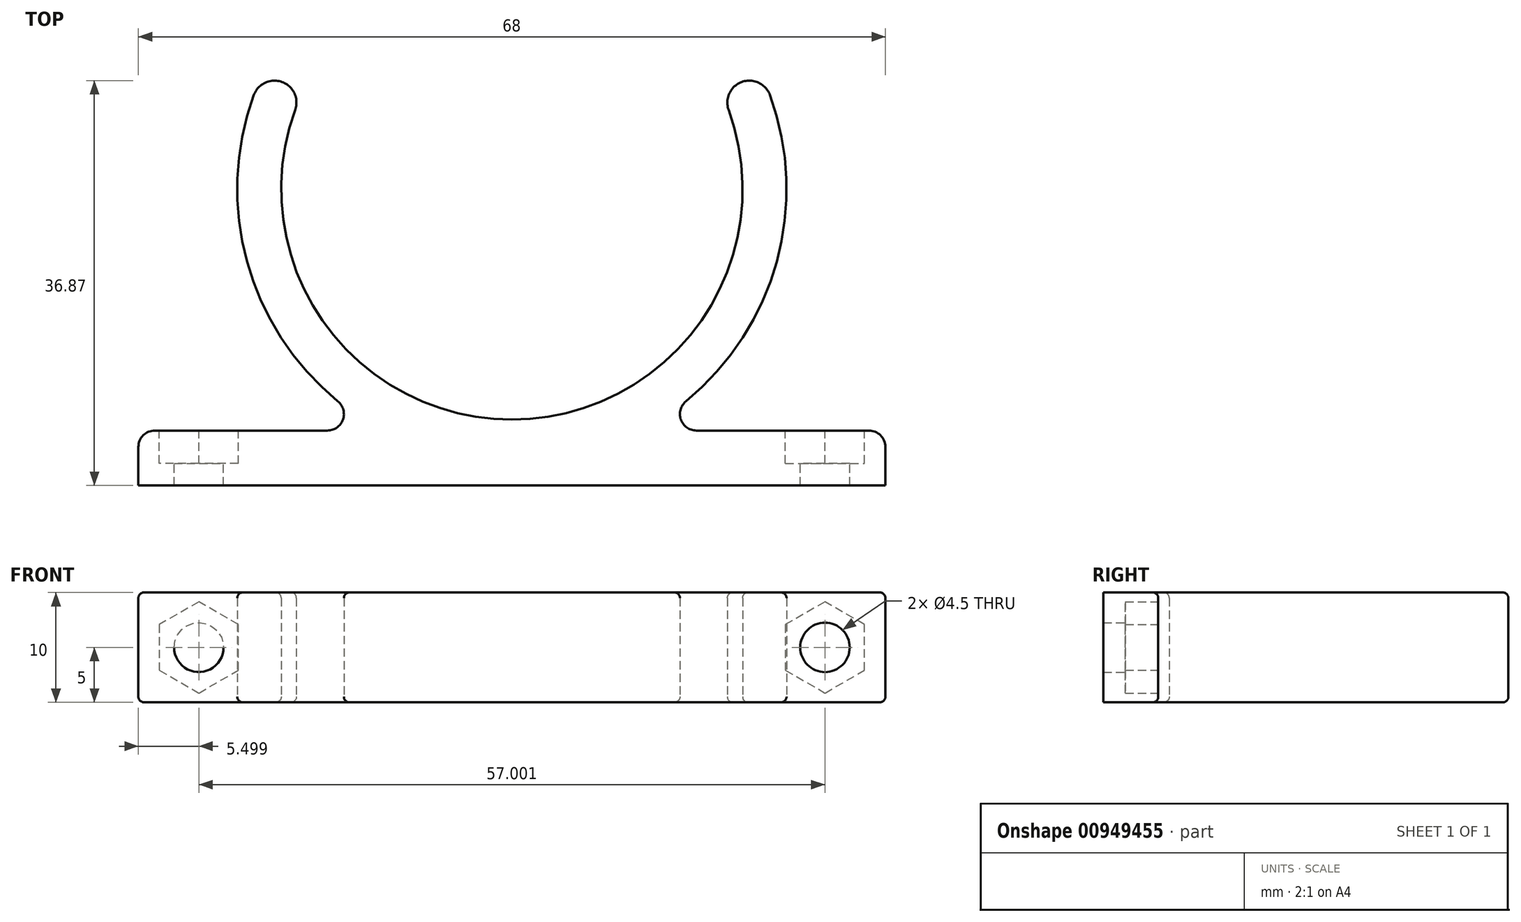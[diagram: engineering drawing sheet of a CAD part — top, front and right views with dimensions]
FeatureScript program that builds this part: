
annotation { "Feature Type Name" : "Feature", "Feature Type Description" : "" }
export const myFeature = defineFeature(function(context is Context, id is Id, definition is map)
    precondition{}
    {
        {
            var Q0;
            Q0=qCreatedBy(makeId("Top.planeOp"),FACE);
            var sketch = newSketch(context, id + "F0", { "sketchPlane" : qUnion([Q0])});
            skArc(sketch, "E0", {"start": v(19.73, 7.18) * mm, "mid": v(0, -21) * mm, "end": v(-19.73, 7.18) * mm});
            skLineSegment(sketch, "E1", {"start": v(0, 0) * mm, "end": v(19.73, 7.18) * mm, "construction": true});
            skLineSegment(sketch, "E2", {"start": v(0, 0) * mm, "end": v(-19.73, 7.18) * mm, "construction": true});
            skArc(sketch, "E3", {"start": v(15.84, -19.34) * mm, "mid": v(24.1, -6.61) * mm, "end": v(23.5, 8.55) * mm});
            skLineSegment(sketch, "E4", {"start": v(0, 0) * mm, "end": v(-23.5, 8.55) * mm, "construction": true});
            skLineSegment(sketch, "E5", {"start": v(0, 0) * mm, "end": v(23.5, 8.55) * mm, "construction": true});
            skLineSegment(sketch, "E6", {"start": v(-23.5, 8.55) * mm, "end": v(-19.73, 7.18) * mm});
            skLineSegment(sketch, "E7", {"start": v(23.5, 8.55) * mm, "end": v(19.73, 7.18) * mm});
            skLineSegment(sketch, "E8.bottom", {"start": v(34, -27) * mm, "end": v(-34, -27) * mm});
            skLineSegment(sketch, "E8.top", {"start": v(32.5, -22) * mm, "end": v(16.8, -22) * mm});
            skLineSegment(sketch, "E8.left", {"start": v(34, -27) * mm, "end": v(34, -23.5) * mm});
            skLineSegment(sketch, "E8.right", {"start": v(-34, -27) * mm, "end": v(-34, -23.5) * mm});
            skPoint(sketch, "E8.middle", {"position": v(0, -24.5) * mm});
            skArc(sketch, "E9", {"start": v(23.5, 8.55) * mm, "mid": v(20.93, 9.75) * mm, "end": v(19.73, 7.18) * mm});
            skArc(sketch, "E10", {"start": v(-23.5, 8.55) * mm, "mid": v(-20.93, 9.75) * mm, "end": v(-19.73, 7.18) * mm});
            skPoint(sketch, "E11.visualSharp", {"position": v(-34, -22) * mm});
            skArc(sketch, "E11.filletArc", {"start": v(-32.5, -22) * mm, "mid": v(-33.56, -22.44) * mm, "end": v(-34, -23.5) * mm});
            skPoint(sketch, "E12.visualSharp", {"position": v(34, -22) * mm});
            skArc(sketch, "E12.filletArc", {"start": v(34, -23.5) * mm, "mid": v(33.56, -22.44) * mm, "end": v(32.5, -22) * mm});
            skArc(sketch, "E13.filletArc", {"start": v(15.84, -19.34) * mm, "mid": v(15.38, -21) * mm, "end": v(16.8, -22) * mm});
            skArc(sketch, "E14", {"start": v(-23.5, 8.55) * mm, "mid": v(-24.1, -6.61) * mm, "end": v(-15.84, -19.34) * mm});
            skLineSegment(sketch, "E15", {"start": v(-32.5, -22) * mm, "end": v(-16.8, -22) * mm});
            skPoint(sketch, "E16.visualSharp", {"position": v(-11.87, -22) * mm});
            skArc(sketch, "E16.filletArc", {"start": v(-16.8, -22) * mm, "mid": v(-15.38, -21) * mm, "end": v(-15.84, -19.34) * mm});
            skSolve(sketch);
        }
        {
            var Q0;
            Q0=makeQuery(id+"F0.imprint","IMPRINT",FACE,{"disambiguationData":[TD([[makeQuery(id+"F0.imprint","IMPRINT",EDGE,{"derivedFrom":sQuery(id+"F0.wireOp",EDGE,"E0")}),1.0]])]});
            var Q1;
            Q1=makeQuery(id+"F0.imprint","IMPRINT",FACE,{"disambiguationData":[TD([[makeQuery(id+"F0.imprint","IMPRINT",EDGE,{"derivedFrom":sQuery(id+"F0.wireOp",EDGE,"E8.bottom")}),-1.0]])]});
            var Q2;
            {var subQ0=sQuery(id+"F0.wireOp",EDGE,"E8.top");var subQ1=sQuery(id+"F0.wireOp",EDGE,"E3");var subQ2=makeQuery(id+"F0.imprint","INTERSECT",VERTEX,{"disambiguationData":[OD(0.0)],"derivedFrom":[subQ1,subQ0]});Q2=makeQuery(id+"F0.imprint","IMPRINT",FACE,{"disambiguationData":[TD([[makeQuery(id+"F0.imprint","IMPRINT",EDGE,{"disambiguationData":[TD([[subQ2,-1.0]])],"derivedFrom":subQ1}),1.0]])]});}
            var Q3;
            Q3=makeQuery(id+"F0.imprint","IMPRINT",FACE,{"disambiguationData":[TD([[makeQuery(id+"F0.imprint","IMPRINT",EDGE,{"derivedFrom":sQuery(id+"F0.wireOp",EDGE,"E6")}),1.0]])]});
            var Q4;
            Q4=makeQuery(id+"F0.imprint","IMPRINT",FACE,{"disambiguationData":[TD([[makeQuery(id+"F0.imprint","IMPRINT",EDGE,{"derivedFrom":sQuery(id+"F0.wireOp",EDGE,"E7")}),-1.0]])]});
            extrude(context, id + "F1", {"entities" : qUnion([Q0, Q1, Q2, Q3, Q4]), "endBound" : BoundingType.SYMMETRIC, "depth" : 10 * mm, "offsetDistance" : 25 * mm});
        }
        {
            var Q0;
            {var subQ0=sQuery(id+"F0.wireOp",EDGE,"E8.top");Q0=makeQuery(id+"F1.opExtrude","SWEPT_FACE",FACE,{"disambiguationData":[OSD([subQ0]),TDD([makeQuery(id+"F0.imprint","IMPRINT",EDGE,{"disambiguationData":[TD([[makeQuery(id+"F0.imprint","INTERSECT",VERTEX,{"derivedFrom":[subQ0,sQuery(id+"F0.wireOp",EDGE,"E12.filletArc")]}),-1.0]])],"derivedFrom":subQ0})])]});}
            var sketch = newSketch(context, id + "F2", { "sketchPlane" : qUnion([Q0])});
            skCircle(sketch, "E17", {"center": v(-28.5, 0) * mm, "radius": 2.25 * mm});
            skSolve(sketch);
        }
        {
            var Q0;
            Q0 = qSketchRegion(id + "F2", true);
            extrude(context, id + "F3", {"entities" : qUnion([Q0]), "operationType" : NewBodyOperationType.REMOVE, "oppositeDirection" : true, "depth" : 25 * mm, "offsetDistance" : 25 * mm});
        }
        {
            var Q0;
            {var subQ0=sQuery(id+"F0.wireOp",EDGE,"E8.top");Q0=makeQuery(id+"F1.opExtrude","SWEPT_FACE",FACE,{"disambiguationData":[OSD([subQ0]),TDD([makeQuery(id+"F0.imprint","IMPRINT",EDGE,{"disambiguationData":[TD([[makeQuery(id+"F0.imprint","INTERSECT",VERTEX,{"derivedFrom":[subQ0,sQuery(id+"F0.wireOp",EDGE,"E12.filletArc")]}),-1.0]])],"derivedFrom":subQ0})])]});}
            var sketch = newSketch(context, id + "F4", { "sketchPlane" : qUnion([Q0])});
            skCircle(sketch, "E18.cCircle", {"center": v(-28.5, 0) * mm, "radius": 3.6 * mm, "construction": true});
            skLineSegment(sketch, "E18.0", {"start": v(-32.1, -2.08) * mm, "end": v(-32.1, 2.08) * mm});
            skLineSegment(sketch, "E18.1", {"start": v(-32.1, 2.08) * mm, "end": v(-28.5, 4.16) * mm});
            skLineSegment(sketch, "E18.2", {"start": v(-28.5, 4.16) * mm, "end": v(-24.9, 2.08) * mm});
            skLineSegment(sketch, "E18.3", {"start": v(-24.9, 2.08) * mm, "end": v(-24.9, -2.08) * mm});
            skLineSegment(sketch, "E18.4", {"start": v(-24.9, -2.08) * mm, "end": v(-28.5, -4.16) * mm});
            skLineSegment(sketch, "E18.5", {"start": v(-28.5, -4.16) * mm, "end": v(-32.1, -2.08) * mm});
            skPoint(sketch, "E18.0.midPoint", {"position": v(-32.1, 0) * mm});
            skSolve(sketch);
        }
        {
            var Q0;
            Q0 = qSketchRegion(id + "F4", true);
            extrude(context, id + "F5", {"entities" : qUnion([Q0]), "operationType" : NewBodyOperationType.REMOVE, "oppositeDirection" : true, "depth" : 3 * mm, "offsetDistance" : 25 * mm});
        }
        {
            var Q0;
            Q0=makeQuery(id+"F1.opExtrude","CAP_EDGE",EDGE,{"disambiguationData":[OSD([sQuery(id+"F0.wireOp",EDGE,"E0")])],"isStart":false});
            var Q1;
            Q1=makeQuery(id+"F1.opExtrude","CAP_EDGE",EDGE,{"disambiguationData":[OSD([sQuery(id+"F0.wireOp",EDGE,"E9")])],"isStart":false});
            var Q2;
            {var subQ0=sQuery(id+"F0.wireOp",EDGE,"E3");Q2=makeQuery(id+"F1.opExtrude","CAP_EDGE",EDGE,{"disambiguationData":[OSD([subQ0]),TDD([makeQuery(id+"F0.imprint","IMPRINT",EDGE,{"disambiguationData":[TD([[makeQuery(id+"F0.imprint","INTERSECT",VERTEX,{"disambiguationData":[OD(1.0)],"derivedFrom":[subQ0,sQuery(id+"F0.wireOp",EDGE,"E8.top")]}),-1.0]])],"derivedFrom":subQ0})])],"isStart":false});}
            var Q3;
            {var subQ0=sQuery(id+"F0.wireOp",EDGE,"E8.top");Q3=makeQuery(id+"F1.opExtrude","CAP_EDGE",EDGE,{"disambiguationData":[OSD([subQ0]),TDD([makeQuery(id+"F0.imprint","IMPRINT",EDGE,{"disambiguationData":[TD([[makeQuery(id+"F0.imprint","INTERSECT",VERTEX,{"derivedFrom":[subQ0,sQuery(id+"F0.wireOp",EDGE,"E12.filletArc")]}),-1.0]])],"derivedFrom":subQ0})])],"isStart":false});}
            var Q4;
            Q4=makeQuery(id+"F1.opExtrude","CAP_EDGE",EDGE,{"disambiguationData":[OSD([sQuery(id+"F0.wireOp",EDGE,"E12.filletArc")])],"isStart":false});
            var Q5;
            Q5=makeQuery(id+"F1.opExtrude","CAP_EDGE",EDGE,{"disambiguationData":[OSD([sQuery(id+"F0.wireOp",EDGE,"E8.left")])],"isStart":false});
            var Q6;
            Q6=makeQuery(id+"F1.opExtrude","CAP_EDGE",EDGE,{"disambiguationData":[OSD([sQuery(id+"F0.wireOp",EDGE,"E10")])],"isStart":false});
            var Q7;
            {var subQ0=sQuery(id+"F0.wireOp",EDGE,"E3");Q7=makeQuery(id+"F1.opExtrude","CAP_EDGE",EDGE,{"disambiguationData":[OSD([subQ0]),TDD([makeQuery(id+"F0.imprint","IMPRINT",EDGE,{"disambiguationData":[TD([[makeQuery(id+"F0.imprint","INTERSECT",VERTEX,{"disambiguationData":[OD(0.0)],"derivedFrom":[subQ0,sQuery(id+"F0.wireOp",EDGE,"E8.top")]}),1.0]])],"derivedFrom":subQ0})])],"isStart":false});}
            var Q8;
            {var subQ0=sQuery(id+"F0.wireOp",EDGE,"E8.top");Q8=makeQuery(id+"F1.opExtrude","CAP_EDGE",EDGE,{"disambiguationData":[OSD([subQ0]),TDD([makeQuery(id+"F0.imprint","IMPRINT",EDGE,{"disambiguationData":[TD([[makeQuery(id+"F0.imprint","INTERSECT",VERTEX,{"derivedFrom":[subQ0,sQuery(id+"F0.wireOp",EDGE,"E11.filletArc")]}),1.0]])],"derivedFrom":subQ0})])],"isStart":false});}
            var Q9;
            Q9=makeQuery(id+"F1.opExtrude","CAP_EDGE",EDGE,{"disambiguationData":[OSD([sQuery(id+"F0.wireOp",EDGE,"E11.filletArc")])],"isStart":false});
            var Q10;
            Q10=makeQuery(id+"F1.opExtrude","CAP_EDGE",EDGE,{"disambiguationData":[OSD([sQuery(id+"F0.wireOp",EDGE,"E8.right")])],"isStart":false});
            fillet(context, id + "F6", {"entities" : qUnion([Q0, Q1, Q2, Q3, Q4, Q5, Q6, Q7, Q8, Q9, Q10]), "radius" : 0.5 * mm, "tangentPropagation" : true, "allowEdgeOverflow" : false});
        }
        {
            var Q0;
            Q0=makeQuery(id+"F1.opExtrude","CAP_EDGE",EDGE,{"disambiguationData":[OSD([sQuery(id+"F0.wireOp",EDGE,"E0")])],"isStart":true});
            var Q1;
            Q1=makeQuery(id+"F1.opExtrude","CAP_EDGE",EDGE,{"disambiguationData":[OSD([sQuery(id+"F0.wireOp",EDGE,"E9")])],"isStart":true});
            var Q2;
            {var subQ0=sQuery(id+"F0.wireOp",EDGE,"E3");Q2=makeQuery(id+"F1.opExtrude","CAP_EDGE",EDGE,{"disambiguationData":[OSD([subQ0]),TDD([makeQuery(id+"F0.imprint","IMPRINT",EDGE,{"disambiguationData":[TD([[makeQuery(id+"F0.imprint","INTERSECT",VERTEX,{"disambiguationData":[OD(1.0)],"derivedFrom":[subQ0,sQuery(id+"F0.wireOp",EDGE,"E8.top")]}),-1.0]])],"derivedFrom":subQ0})])],"isStart":true});}
            var Q3;
            {var subQ0=sQuery(id+"F0.wireOp",EDGE,"E8.top");Q3=makeQuery(id+"F1.opExtrude","CAP_EDGE",EDGE,{"disambiguationData":[OSD([subQ0]),TDD([makeQuery(id+"F0.imprint","IMPRINT",EDGE,{"disambiguationData":[TD([[makeQuery(id+"F0.imprint","INTERSECT",VERTEX,{"derivedFrom":[subQ0,sQuery(id+"F0.wireOp",EDGE,"E12.filletArc")]}),-1.0]])],"derivedFrom":subQ0})])],"isStart":true});}
            var Q4;
            Q4=makeQuery(id+"F1.opExtrude","CAP_EDGE",EDGE,{"disambiguationData":[OSD([sQuery(id+"F0.wireOp",EDGE,"E12.filletArc")])],"isStart":true});
            var Q5;
            Q5=makeQuery(id+"F1.opExtrude","CAP_EDGE",EDGE,{"disambiguationData":[OSD([sQuery(id+"F0.wireOp",EDGE,"E8.left")])],"isStart":true});
            var Q6;
            Q6=makeQuery(id+"F1.opExtrude","CAP_EDGE",EDGE,{"disambiguationData":[OSD([sQuery(id+"F0.wireOp",EDGE,"E10")])],"isStart":true});
            var Q7;
            {var subQ0=sQuery(id+"F0.wireOp",EDGE,"E3");Q7=makeQuery(id+"F1.opExtrude","CAP_EDGE",EDGE,{"disambiguationData":[OSD([subQ0]),TDD([makeQuery(id+"F0.imprint","IMPRINT",EDGE,{"disambiguationData":[TD([[makeQuery(id+"F0.imprint","INTERSECT",VERTEX,{"disambiguationData":[OD(0.0)],"derivedFrom":[subQ0,sQuery(id+"F0.wireOp",EDGE,"E8.top")]}),1.0]])],"derivedFrom":subQ0})])],"isStart":true});}
            var Q8;
            {var subQ0=sQuery(id+"F0.wireOp",EDGE,"E8.top");Q8=makeQuery(id+"F1.opExtrude","CAP_EDGE",EDGE,{"disambiguationData":[OSD([subQ0]),TDD([makeQuery(id+"F0.imprint","IMPRINT",EDGE,{"disambiguationData":[TD([[makeQuery(id+"F0.imprint","INTERSECT",VERTEX,{"derivedFrom":[subQ0,sQuery(id+"F0.wireOp",EDGE,"E11.filletArc")]}),1.0]])],"derivedFrom":subQ0})])],"isStart":true});}
            var Q9;
            Q9=makeQuery(id+"F1.opExtrude","CAP_EDGE",EDGE,{"disambiguationData":[OSD([sQuery(id+"F0.wireOp",EDGE,"E11.filletArc")])],"isStart":true});
            var Q10;
            Q10=makeQuery(id+"F1.opExtrude","CAP_EDGE",EDGE,{"disambiguationData":[OSD([sQuery(id+"F0.wireOp",EDGE,"E8.right")])],"isStart":true});
            fillet(context, id + "F7", {"entities" : qUnion([Q0, Q1, Q2, Q3, Q4, Q5, Q6, Q7, Q8, Q9, Q10]), "radius" : 0.5 * mm, "tangentPropagation" : true, "allowEdgeOverflow" : false});
        }
        {
            var Q0;
            Q0=makeQuery(id+"F1.opExtrude","SWEPT_FACE",FACE,{"disambiguationData":[OSD([sQuery(id+"F0.wireOp",EDGE,"E15")])]});
            var sketch = newSketch(context, id + "F8", { "sketchPlane" : qUnion([Q0])});
            skCircle(sketch, "E19", {"center": v(28.5, 0) * mm, "radius": 2.25 * mm});
            skSolve(sketch);
        }
        {
            var Q0;
            Q0 = qSketchRegion(id + "F8", true);
            extrude(context, id + "F9", {"entities" : qUnion([Q0]), "operationType" : NewBodyOperationType.REMOVE, "oppositeDirection" : true, "depth" : 25 * mm, "offsetDistance" : 25 * mm});
        }
        {
            var Q0;
            Q0=makeQuery(id+"F1.opExtrude","SWEPT_FACE",FACE,{"disambiguationData":[OSD([sQuery(id+"F0.wireOp",EDGE,"E15")])]});
            var sketch = newSketch(context, id + "F10", { "sketchPlane" : qUnion([Q0])});
            skCircle(sketch, "E20.cCircle", {"center": v(28.5, 0) * mm, "radius": 3.6 * mm, "construction": true});
            skLineSegment(sketch, "E20.0", {"start": v(32.1, 2.08) * mm, "end": v(32.1, -2.08) * mm});
            skLineSegment(sketch, "E20.1", {"start": v(32.1, -2.08) * mm, "end": v(28.5, -4.16) * mm});
            skLineSegment(sketch, "E20.2", {"start": v(28.5, -4.16) * mm, "end": v(24.9, -2.08) * mm});
            skLineSegment(sketch, "E20.3", {"start": v(24.9, -2.08) * mm, "end": v(24.9, 2.08) * mm});
            skLineSegment(sketch, "E20.4", {"start": v(24.9, 2.08) * mm, "end": v(28.5, 4.16) * mm});
            skLineSegment(sketch, "E20.5", {"start": v(28.5, 4.16) * mm, "end": v(32.1, 2.08) * mm});
            skPoint(sketch, "E20.0.midPoint", {"position": v(32.1, 0) * mm});
            skSolve(sketch);
        }
        {
            var Q0;
            Q0 = qSketchRegion(id + "F10", true);
            extrude(context, id + "F11", {"entities" : qUnion([Q0]), "operationType" : NewBodyOperationType.REMOVE, "oppositeDirection" : true, "depth" : 3 * mm, "offsetDistance" : 25 * mm});
        }
    });
